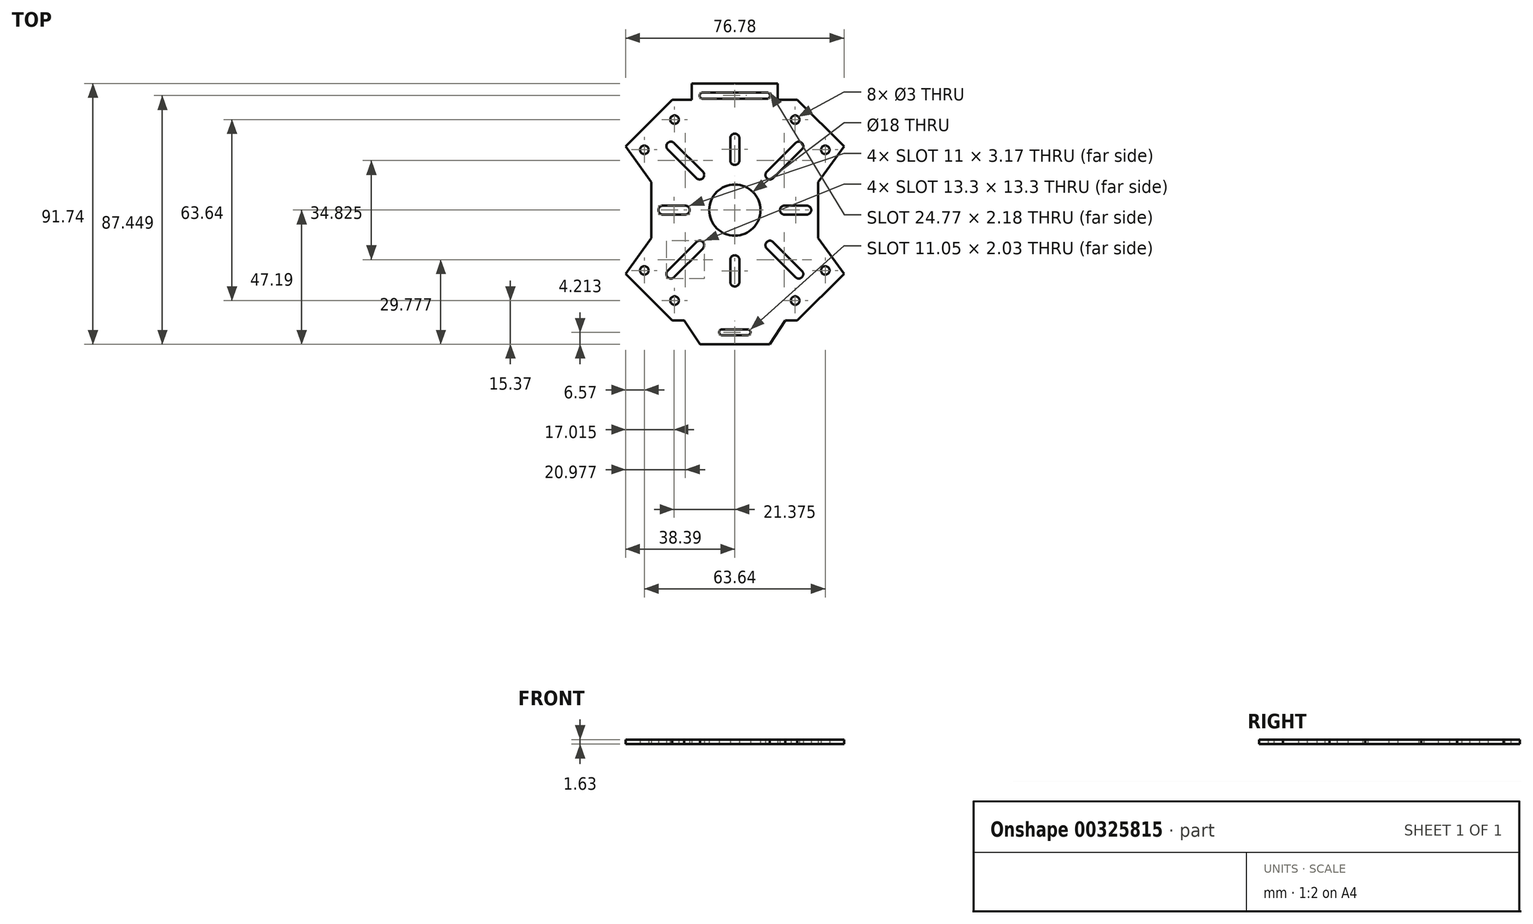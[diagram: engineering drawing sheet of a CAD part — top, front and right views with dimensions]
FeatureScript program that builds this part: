
annotation { "Feature Type Name" : "Feature", "Feature Type Description" : "" }
export const myFeature = defineFeature(function(context is Context, id is Id, definition is map)
    precondition{}
    {
        {
            var Q0;
            Q0=qCreatedBy(makeId("Top.planeOp"),FACE);
            var sketch = newSketch(context, id + "F0", { "sketchPlane" : qUnion([Q0])});
            skCircle(sketch, "E0", {"center": v(0, 0) * mm, "radius": 9 * mm});
            skLineSegment(sketch, "E1", {"start": v(0, 0) * mm, "end": v(0, 78.14) * mm, "construction": true});
            skLineSegment(sketch, "E2", {"start": v(0, 0) * mm, "end": v(-110.17, 0) * mm, "construction": true});
            skLineSegment(sketch, "E3.left", {"start": v(-1.59, 25.29) * mm, "end": v(-1.59, 17.46) * mm});
            skLineSegment(sketch, "E3.right", {"start": v(1.59, 25.29) * mm, "end": v(1.59, 17.46) * mm});
            skArc(sketch, "E4", {"start": v(1.59, 25.29) * mm, "mid": v(0, 26.87) * mm, "end": v(-1.59, 25.29) * mm});
            skArc(sketch, "E5", {"start": v(-1.59, 17.46) * mm, "mid": v(0, 15.88) * mm, "end": v(1.59, 17.46) * mm});
            skLineSegment(sketch, "E6.1.0", {"start": v(-25.29, -1.59) * mm, "end": v(-17.46, -1.59) * mm});
            skLineSegment(sketch, "E6.1.1", {"start": v(-25.29, 1.59) * mm, "end": v(-17.46, 1.59) * mm});
            skArc(sketch, "E6.1.2", {"start": v(-17.46, -1.59) * mm, "mid": v(-15.88, 0) * mm, "end": v(-17.46, 1.59) * mm});
            skArc(sketch, "E6.1.3", {"start": v(-25.29, 1.59) * mm, "mid": v(-26.87, 0) * mm, "end": v(-25.29, -1.59) * mm});
            skLineSegment(sketch, "E6.2.0", {"start": v(1.59, -25.29) * mm, "end": v(1.59, -17.46) * mm});
            skLineSegment(sketch, "E6.2.1", {"start": v(-1.59, -25.29) * mm, "end": v(-1.59, -17.46) * mm});
            skArc(sketch, "E6.2.2", {"start": v(1.59, -17.46) * mm, "mid": v(0, -15.88) * mm, "end": v(-1.59, -17.46) * mm});
            skArc(sketch, "E6.2.3", {"start": v(-1.59, -25.29) * mm, "mid": v(0, -26.87) * mm, "end": v(1.59, -25.29) * mm});
            skLineSegment(sketch, "E6.3.0", {"start": v(25.29, 1.59) * mm, "end": v(17.46, 1.59) * mm});
            skLineSegment(sketch, "E6.3.1", {"start": v(25.29, -1.59) * mm, "end": v(17.46, -1.59) * mm});
            skArc(sketch, "E6.3.2", {"start": v(17.46, 1.59) * mm, "mid": v(15.88, 0) * mm, "end": v(17.46, -1.59) * mm});
            skArc(sketch, "E6.3.3", {"start": v(25.29, -1.59) * mm, "mid": v(26.87, 0) * mm, "end": v(25.29, 1.59) * mm});
            skLineSegment(sketch, "E7", {"start": v(0, 0) * mm, "end": v(-50.05, 50.05) * mm, "construction": true});
            skLineSegment(sketch, "E8.1.0", {"start": v(-23.6, 21.35) * mm, "end": v(-13.47, 11.23) * mm});
            skLineSegment(sketch, "E8.1.1", {"start": v(-21.35, 23.6) * mm, "end": v(-11.23, 13.47) * mm});
            skArc(sketch, "E8.1.2", {"start": v(-13.47, 11.23) * mm, "mid": v(-11.23, 11.23) * mm, "end": v(-11.23, 13.47) * mm});
            skArc(sketch, "E8.1.3", {"start": v(-21.35, 23.6) * mm, "mid": v(-23.6, 23.6) * mm, "end": v(-23.6, 21.35) * mm});
            skArc(sketch, "E9.1.0", {"start": v(-23.6, -21.35) * mm, "mid": v(-23.6, -23.6) * mm, "end": v(-21.35, -23.6) * mm});
            skArc(sketch, "E9.1.1", {"start": v(-11.23, -13.47) * mm, "mid": v(-11.23, -11.23) * mm, "end": v(-13.47, -11.23) * mm});
            skLineSegment(sketch, "E9.1.2", {"start": v(-21.35, -23.6) * mm, "end": v(-11.23, -13.47) * mm});
            skLineSegment(sketch, "E9.1.3", {"start": v(-23.6, -21.35) * mm, "end": v(-13.47, -11.23) * mm});
            skArc(sketch, "E9.2.0", {"start": v(21.35, -23.6) * mm, "mid": v(23.6, -23.6) * mm, "end": v(23.6, -21.35) * mm});
            skArc(sketch, "E9.2.1", {"start": v(13.47, -11.23) * mm, "mid": v(11.23, -11.23) * mm, "end": v(11.23, -13.47) * mm});
            skLineSegment(sketch, "E9.2.2", {"start": v(23.6, -21.35) * mm, "end": v(13.47, -11.23) * mm});
            skLineSegment(sketch, "E9.2.3", {"start": v(21.35, -23.6) * mm, "end": v(11.23, -13.47) * mm});
            skArc(sketch, "E9.3.0", {"start": v(23.6, 21.35) * mm, "mid": v(23.6, 23.6) * mm, "end": v(21.35, 23.6) * mm});
            skArc(sketch, "E9.3.1", {"start": v(11.23, 13.47) * mm, "mid": v(11.23, 11.23) * mm, "end": v(13.47, 11.23) * mm});
            skLineSegment(sketch, "E9.3.2", {"start": v(21.35, 23.6) * mm, "end": v(11.23, 13.47) * mm});
            skLineSegment(sketch, "E9.3.3", {"start": v(23.6, 21.35) * mm, "end": v(13.47, 11.23) * mm});
            skLineSegment(sketch, "E10", {"start": v(-29.34, -9.84) * mm, "end": v(-29.34, 9.84) * mm});
            skLineSegment(sketch, "E11", {"start": v(-29.34, 9.84) * mm, "end": v(-38.4, 22.4) * mm});
            skLineSegment(sketch, "E12", {"start": v(-38.4, 22.4) * mm, "end": v(-21.96, 38.84) * mm});
            skLineSegment(sketch, "E13", {"start": v(-21.96, 38.84) * mm, "end": v(-15.11, 38.84) * mm});
            skLineSegment(sketch, "E14", {"start": v(-15.11, 38.84) * mm, "end": v(-15.11, 44.55) * mm});
            skLineSegment(sketch, "E15", {"start": v(-15.11, 44.55) * mm, "end": v(0, 44.55) * mm});
            skLineSegment(sketch, "E16", {"start": v(-29.34, -9.84) * mm, "end": v(-38.4, -22.4) * mm});
            skLineSegment(sketch, "E17", {"start": v(-38.4, -22.4) * mm, "end": v(-21.96, -38.84) * mm});
            skLineSegment(sketch, "E18", {"start": v(-21.96, -38.84) * mm, "end": v(-17.78, -38.84) * mm});
            skLineSegment(sketch, "E19", {"start": v(-12.26, -47.2) * mm, "end": v(-17.78, -38.84) * mm});
            skLineSegment(sketch, "E20", {"start": v(-12.26, -47.2) * mm, "end": v(0, -47.2) * mm});
            skLineSegment(sketch, "E21.MirrorCS", {"start": v(15.11, 44.55) * mm, "end": v(0, 44.55) * mm});
            skLineSegment(sketch, "E22.MirrorCS", {"start": v(15.11, 38.84) * mm, "end": v(15.11, 44.55) * mm});
            skLineSegment(sketch, "E23.MirrorCS", {"start": v(21.96, 38.84) * mm, "end": v(15.11, 38.84) * mm});
            skLineSegment(sketch, "E24.MirrorCS", {"start": v(38.4, 22.4) * mm, "end": v(21.96, 38.84) * mm});
            skLineSegment(sketch, "E25.MirrorCS", {"start": v(29.34, 9.84) * mm, "end": v(38.4, 22.4) * mm});
            skLineSegment(sketch, "E26.MirrorCS", {"start": v(29.34, -9.84) * mm, "end": v(29.34, 9.84) * mm});
            skLineSegment(sketch, "E27.MirrorCS", {"start": v(29.34, -9.84) * mm, "end": v(38.4, -22.4) * mm});
            skLineSegment(sketch, "E28.MirrorCS", {"start": v(38.4, -22.4) * mm, "end": v(21.96, -38.84) * mm});
            skLineSegment(sketch, "E29.MirrorCS", {"start": v(21.96, -38.84) * mm, "end": v(17.78, -38.84) * mm});
            skLineSegment(sketch, "E30.MirrorCS", {"start": v(12.26, -47.2) * mm, "end": v(17.78, -38.84) * mm});
            skLineSegment(sketch, "E31.MirrorCS", {"start": v(12.26, -47.2) * mm, "end": v(0, -47.2) * mm});
            skLineSegment(sketch, "E32.bottom", {"start": v(-11.3, 41.35) * mm, "end": v(11.3, 41.35) * mm});
            skLineSegment(sketch, "E32.top", {"start": v(-11.3, 39.17) * mm, "end": v(11.3, 39.17) * mm});
            skLineSegment(sketch, "E33.bottom", {"start": v(-4.5, -41.96) * mm, "end": v(4.5, -41.96) * mm});
            skLineSegment(sketch, "E33.top", {"start": v(-4.5, -44) * mm, "end": v(4.5, -44) * mm});
            skArc(sketch, "E34", {"start": v(-11.3, 41.35) * mm, "mid": v(-12.38, 40.26) * mm, "end": v(-11.3, 39.17) * mm});
            skArc(sketch, "E35", {"start": v(11.3, 39.17) * mm, "mid": v(12.38, 40.26) * mm, "end": v(11.3, 41.35) * mm});
            skArc(sketch, "E36", {"start": v(-4.5, -41.96) * mm, "mid": v(-5.52, -42.98) * mm, "end": v(-4.5, -44) * mm});
            skArc(sketch, "E37", {"start": v(4.5, -44) * mm, "mid": v(5.52, -42.98) * mm, "end": v(4.5, -41.96) * mm});
            skCircle(sketch, "E38", {"center": v(-21.21, 31.82) * mm, "radius": 1.5 * mm});
            skCircle(sketch, "E39", {"center": v(-31.82, 21.21) * mm, "radius": 1.5 * mm});
            skLineSegment(sketch, "E40", {"start": v(-19.53, 33.5) * mm, "end": v(-34.67, 18.36) * mm, "construction": true});
            skCircle(sketch, "E41.1.0", {"center": v(-31.82, -21.21) * mm, "radius": 1.5 * mm});
            skCircle(sketch, "E41.1.1", {"center": v(-21.21, -31.82) * mm, "radius": 1.5 * mm});
            skCircle(sketch, "E41.2.0", {"center": v(21.21, -31.82) * mm, "radius": 1.5 * mm});
            skCircle(sketch, "E41.2.1", {"center": v(31.82, -21.21) * mm, "radius": 1.5 * mm});
            skCircle(sketch, "E41.3.0", {"center": v(31.82, 21.21) * mm, "radius": 1.5 * mm});
            skCircle(sketch, "E41.3.1", {"center": v(21.21, 31.82) * mm, "radius": 1.5 * mm});
            skSolve(sketch);
        }
        {
            var Q0;
            Q0=makeQuery(id+"F0.imprint","IMPRINT",FACE,{"disambiguationData":[TD([[makeQuery(id+"F0.imprint","IMPRINT",EDGE,{"derivedFrom":sQuery(id+"F0.wireOp",EDGE,"E0")}),-1.0]])]});
            extrude(context, id + "F1", {"entities" : qUnion([Q0]), "depth" : 1.63 * mm});
        }
    });
